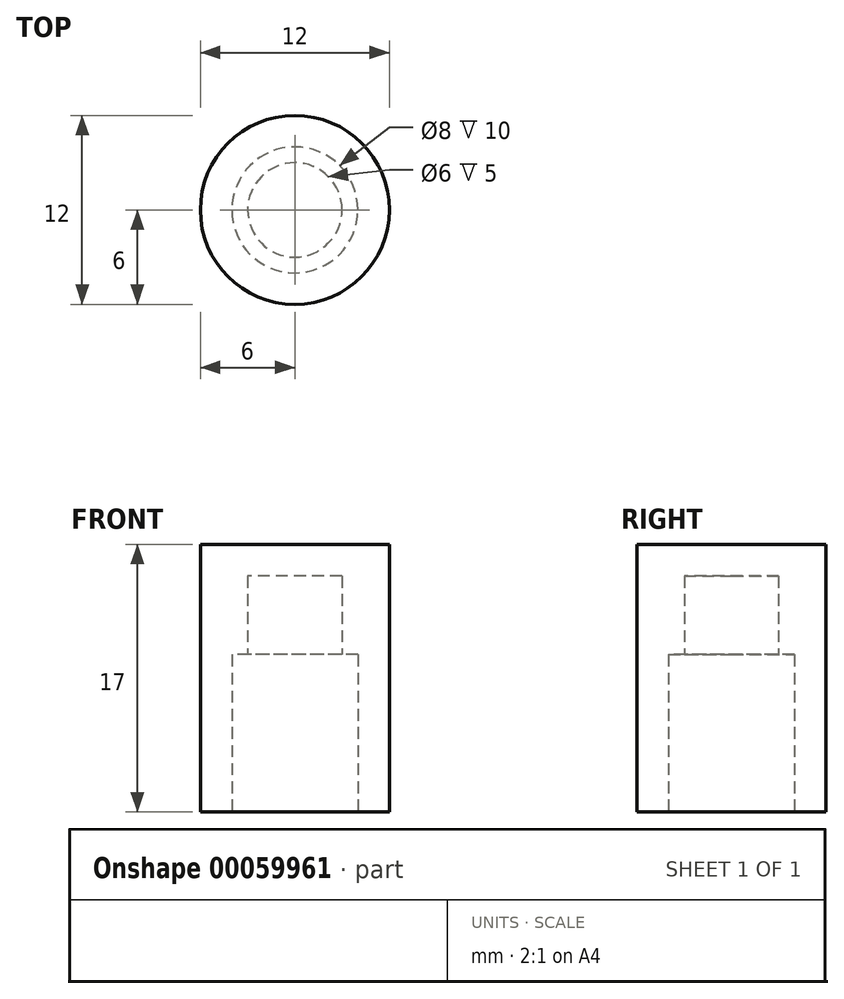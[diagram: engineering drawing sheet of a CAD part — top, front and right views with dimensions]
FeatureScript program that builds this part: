
annotation { "Feature Type Name" : "Feature", "Feature Type Description" : "" }
export const myFeature = defineFeature(function(context is Context, id is Id, definition is map)
    precondition{}
    {
        {
            var Q0;
            Q0=qCreatedBy(makeId("Top.planeOp"),FACE);
            var sketch = newSketch(context, id + "F0", { "sketchPlane" : qUnion([Q0])});
            skCircle(sketch, "E0", {"center": v(0, 0) * mm, "radius": 6 * mm});
            skCircle(sketch, "E1", {"center": v(0, 0) * mm, "radius": 4 * mm});
            skSolve(sketch);
        }
        {
            var Q0;
            Q0=makeQuery(id+"F0.imprint","IMPRINT",FACE,{"disambiguationData":[TD([[makeQuery(id+"F0.imprint","IMPRINT",EDGE,{"derivedFrom":sQuery(id+"F0.wireOp",EDGE,"E0")}),1.0]])]});
            extrude(context, id + "F1", {"entities" : qUnion([Q0]), "depth" : 10 * mm});
        }
        {
            var Q0;
            Q0=makeQuery(id+"F1.opExtrude","CAP_FACE",FACE,{"disambiguationData":[OSD([sQuery(id+"F0.wireOp",EDGE,"E0"),sQuery(id+"F0.wireOp",EDGE,"E1")])],"isStart":false});
            var sketch = newSketch(context, id + "F2", { "sketchPlane" : qUnion([Q0])});
            skCircle(sketch, "E2", {"center": v(0, 0) * mm, "radius": 3 * mm});
            skCircle(sketch, "E3", {"center": v(0, 0) * mm, "radius": 152.4 * mm});
            skCircle(sketch, "E4", {"center": v(0, 0) * mm, "radius": 6 * mm});
            skSolve(sketch);
        }
        {
            var Q0;
            Q0=makeQuery(id+"F2.imprint","IMPRINT",FACE,{"disambiguationData":[TD([[makeQuery(id+"F2.imprint","IMPRINT",EDGE,{"derivedFrom":sQuery(id+"F2.wireOp",EDGE,"E2")}),-1.0]])]});
            var Q1;
            Q1=makeQuery(id+"F2.imprint","IMPRINT",FACE,{"disambiguationData":[TD([[makeQuery(id+"F2.imprint","IMPRINT",EDGE,{"derivedFrom":sQuery(id+"F2.wireOp",EDGE,"E4")}),1.0]])]});
            extrude(context, id + "F3", {"entities" : qUnion([Q0, Q1]), "operationType" : NewBodyOperationType.ADD, "depth" : 5 * mm});
        }
        {
            var Q0;
            Q0=makeQuery(id+"F3.opExtrude","CAP_FACE",FACE,{"disambiguationData":[OSD([sQuery(id+"F2.wireOp",EDGE,"E2"),sQuery(id+"F2.wireOp",EDGE,"E4")])],"isStart":false});
            var sketch = newSketch(context, id + "F4", { "sketchPlane" : qUnion([Q0])});
            skCircle(sketch, "E5", {"center": v(0, 0) * mm, "radius": 6 * mm});
            skSolve(sketch);
        }
        {
            var Q0;
            Q0=makeQuery(id+"F4.imprint","IMPRINT",FACE,{"disambiguationData":[TD([[makeQuery(id+"F4.imprint","IMPRINT",EDGE,{"derivedFrom":sQuery(id+"F4.wireOp",EDGE,"E5")}),1.0]])]});
            var Q1;
            Q1=makeQuery(id+"F4.imprint","IMPRINT",FACE,{"disambiguationData":[TD([[makeQuery(id+"F4.imprint","IMPRINT",EDGE,{"derivedFrom":makeQuery(id+"F3.opExtrude","CAP_EDGE",EDGE,{"disambiguationData":[OSD([sQuery(id+"F2.wireOp",EDGE,"E2")])],"isStart":false})}),1.0]])]});
            extrude(context, id + "F5", {"entities" : qUnion([Q0, Q1]), "operationType" : NewBodyOperationType.ADD, "depth" : 2 * mm});
        }
    });
